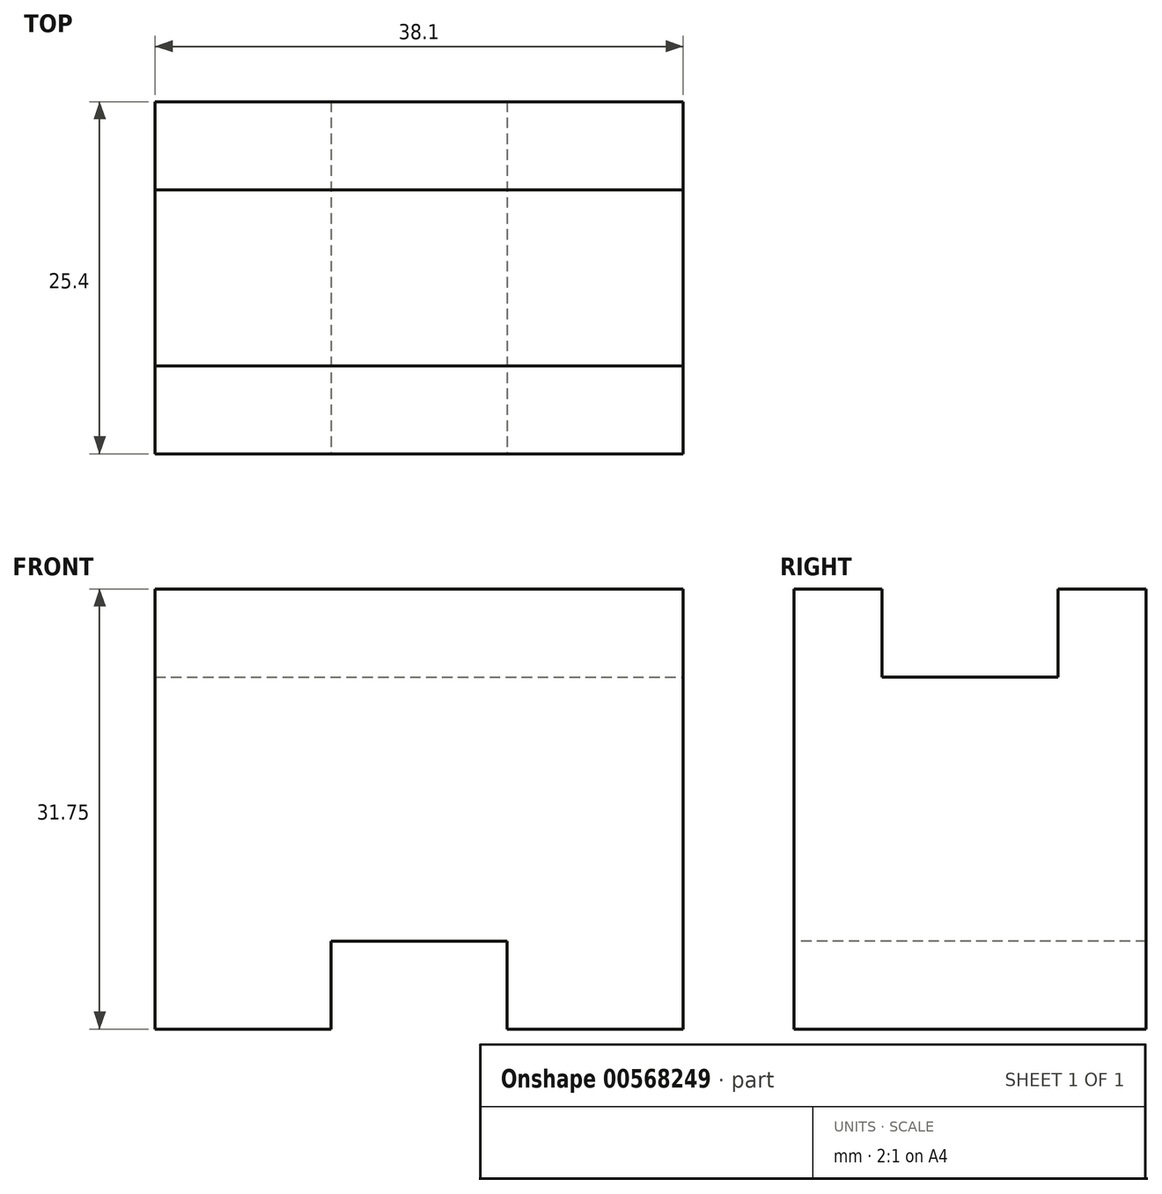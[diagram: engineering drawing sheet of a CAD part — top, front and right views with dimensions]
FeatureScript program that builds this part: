
annotation { "Feature Type Name" : "Feature", "Feature Type Description" : "" }
export const myFeature = defineFeature(function(context is Context, id is Id, definition is map)
    precondition{}
    {
        {
            var Q0;
            Q0=qCreatedBy(makeId("Front.planeOp"),FACE);
            var sketch = newSketch(context, id + "F0", { "sketchPlane" : qUnion([Q0])});
            skLineSegment(sketch, "E0", {"start": v(0, 0) * mm, "end": v(-12.7, 0) * mm});
            skLineSegment(sketch, "E1", {"start": v(-12.7, 0) * mm, "end": v(-12.7, 6.35) * mm});
            skLineSegment(sketch, "E2", {"start": v(-12.7, 6.35) * mm, "end": v(-25.4, 6.35) * mm});
            skLineSegment(sketch, "E3", {"start": v(-25.4, 6.35) * mm, "end": v(-25.4, 0) * mm});
            skLineSegment(sketch, "E4", {"start": v(-25.4, 0) * mm, "end": v(-38.1, 0) * mm});
            skLineSegment(sketch, "E5", {"start": v(-38.1, 0) * mm, "end": v(-38.1, 31.75) * mm});
            skLineSegment(sketch, "E6", {"start": v(-38.1, 31.75) * mm, "end": v(0, 31.75) * mm});
            skLineSegment(sketch, "E7", {"start": v(0, 31.75) * mm, "end": v(0, 0) * mm});
            skSolve(sketch);
        }
        {
            var Q0;
            Q0=qSketchRegion(id+"F0",true);
            extrude(context, id + "F1", {"entities" : qUnion([Q0]), "oppositeDirection" : true, "depth" : 25.4 * mm});
        }
        {
            var Q0;
            Q0=makeQuery(id+"F1.opExtrude","SWEPT_FACE",FACE,{"disambiguationData":[OSD([sQuery(id+"F0.wireOp",EDGE,"E7")])]});
            var sketch = newSketch(context, id + "F2", { "sketchPlane" : qUnion([Q0])});
            skLineSegment(sketch, "E8", {"start": v(0, 31.75) * mm, "end": v(6.35, 31.75) * mm});
            skLineSegment(sketch, "E9", {"start": v(6.35, 31.75) * mm, "end": v(6.35, 25.4) * mm});
            skLineSegment(sketch, "E10", {"start": v(6.35, 25.4) * mm, "end": v(19.05, 25.4) * mm});
            skLineSegment(sketch, "E11", {"start": v(19.05, 25.4) * mm, "end": v(19.05, 31.75) * mm});
            skLineSegment(sketch, "E12", {"start": v(19.05, 31.75) * mm, "end": v(6.35, 31.75) * mm});
            skSolve(sketch);
        }
        {
            var Q0;
            Q0=qSketchRegion(id+"F2",true);
            extrude(context, id + "F3", {"entities" : qUnion([Q0]), "operationType" : NewBodyOperationType.REMOVE, "oppositeDirection" : true, "depth" : 38.1 * mm});
        }
    });
